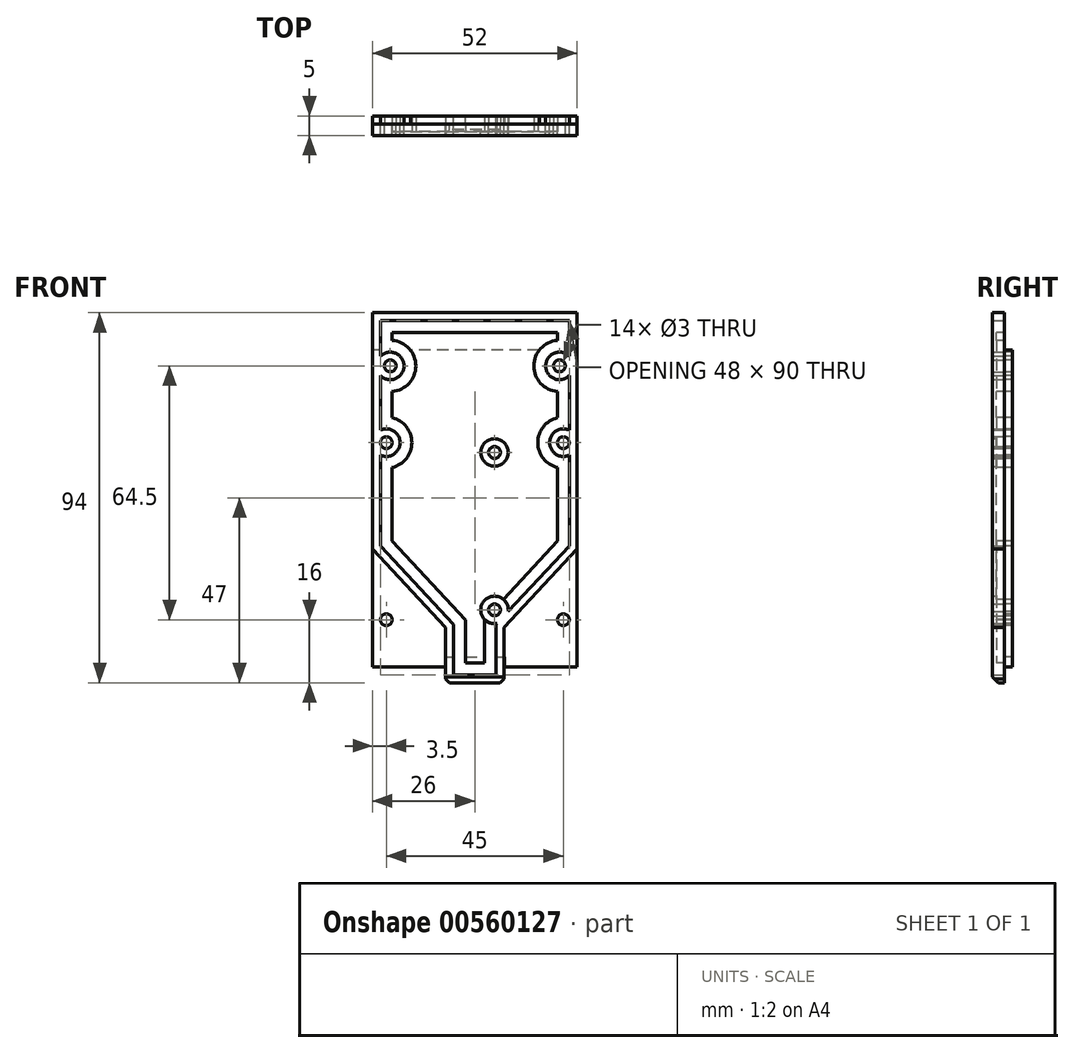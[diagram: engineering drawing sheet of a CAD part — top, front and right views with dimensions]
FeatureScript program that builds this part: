
annotation { "Feature Type Name" : "Feature", "Feature Type Description" : "" }
export const myFeature = defineFeature(function(context is Context, id is Id, definition is map)
    precondition{}
    {
        {
            var Q0;
            Q0=qCreatedBy(makeId("Front.planeOp"),FACE);
            var sketch = newSketch(context, id + "F0", { "sketchPlane" : qUnion([Q0])});
            skLineSegment(sketch, "E0.bottom", {"start": v(26, 40.25) * mm, "end": v(-26, 40.25) * mm});
            skLineSegment(sketch, "E0.top", {"start": v(26, -40.25) * mm, "end": v(-26, -40.25) * mm});
            skLineSegment(sketch, "E0.left", {"start": v(26, 40.25) * mm, "end": v(26, -40.25) * mm});
            skLineSegment(sketch, "E0.right", {"start": v(-26, 40.25) * mm, "end": v(-26, -40.25) * mm});
            skPoint(sketch, "E0.middle", {"position": v(0, 0) * mm});
            skCircle(sketch, "E1", {"center": v(-21.5, 36.25) * mm, "radius": 1.5 * mm});
            skCircle(sketch, "E2", {"center": v(-22.5, 16.75) * mm, "radius": 1.5 * mm});
            skCircle(sketch, "E3", {"center": v(-22.5, -28.25) * mm, "radius": 1.5 * mm});
            skCircle(sketch, "E4.MirrorC", {"center": v(22.5, -28.25) * mm, "radius": 1.5 * mm});
            skCircle(sketch, "E5.MirrorC", {"center": v(22.5, 16.75) * mm, "radius": 1.5 * mm});
            skCircle(sketch, "E6.MirrorC", {"center": v(21.5, 36.25) * mm, "radius": 1.5 * mm});
            skLineSegment(sketch, "E7.bottom", {"start": v(-7.5, -37.75) * mm, "end": v(7.5, -37.75) * mm});
            skLineSegment(sketch, "E7.top", {"start": v(-7.5, -40.25) * mm, "end": v(7.5, -40.25) * mm});
            skLineSegment(sketch, "E7.left", {"start": v(-7.5, -37.75) * mm, "end": v(-7.5, -40.25) * mm});
            skLineSegment(sketch, "E7.right", {"start": v(7.5, -37.75) * mm, "end": v(7.5, -40.25) * mm});
            skCircle(sketch, "E8", {"center": v(5, 14.25) * mm, "radius": 1.5 * mm});
            skCircle(sketch, "E9", {"center": v(5, -25.75) * mm, "radius": 1.5 * mm});
            skSolve(sketch);
        }
        {
            var Q0;
            Q0=makeQuery(id+"F0.imprint","IMPRINT",FACE,{"disambiguationData":[TD([[makeQuery(id+"F0.imprint","IMPRINT",EDGE,{"derivedFrom":sQuery(id+"F0.wireOp",EDGE,"E0.bottom")}),1.0]])]});
            extrude(context, id + "F1", {"entities" : qUnion([Q0]), "oppositeDirection" : true, "depth" : 2 * mm, "offsetDistance" : 25 * mm});
        }
        {
            var Q0;
            Q0=makeQuery(id+"F1.opExtrude","CAP_FACE",FACE,{"disambiguationData":[OSD([sQuery(id+"F0.wireOp",EDGE,"E0.bottom"),sQuery(id+"F0.wireOp",EDGE,"E0.top"),sQuery(id+"F0.wireOp",EDGE,"E0.left"),sQuery(id+"F0.wireOp",EDGE,"E0.right"),sQuery(id+"F0.wireOp",EDGE,"E1"),sQuery(id+"F0.wireOp",EDGE,"E2"),sQuery(id+"F0.wireOp",EDGE,"E3"),sQuery(id+"F0.wireOp",EDGE,"E4.MirrorC"),sQuery(id+"F0.wireOp",EDGE,"E5.MirrorC"),sQuery(id+"F0.wireOp",EDGE,"E6.MirrorC"),sQuery(id+"F0.wireOp",EDGE,"E7.bottom"),sQuery(id+"F0.wireOp",EDGE,"E7.left"),sQuery(id+"F0.wireOp",EDGE,"E7.right")])],"isStart":true});
            var sketch = newSketch(context, id + "F2", { "sketchPlane" : qUnion([Q0])});
            skLineSegment(sketch, "E10.bottom", {"start": v(-26, -40.25) * mm, "end": v(26, -40.25) * mm});
            skLineSegment(sketch, "E10.top", {"start": v(-26, 49.75) * mm, "end": v(26, 49.75) * mm});
            skLineSegment(sketch, "E10.left", {"start": v(-26, -40.25) * mm, "end": v(-26, 49.75) * mm});
            skLineSegment(sketch, "E10.right", {"start": v(26, -40.25) * mm, "end": v(26, 49.75) * mm});
            skLineSegment(sketch, "E11", {"start": v(-26, -10.25) * mm, "end": v(-7.4, -30.25) * mm});
            skLineSegment(sketch, "E12", {"start": v(-7.4, -30.25) * mm, "end": v(-7.4, -44.25) * mm});
            skLineSegment(sketch, "E13", {"start": v(-7.4, -44.25) * mm, "end": v(0, -44.25) * mm});
            skLineSegment(sketch, "E14.MirrorCS", {"start": v(26, -10.25) * mm, "end": v(7.4, -30.25) * mm});
            skLineSegment(sketch, "E15.MirrorCS", {"start": v(7.4, -30.25) * mm, "end": v(7.4, -44.25) * mm});
            skLineSegment(sketch, "E16.MirrorCS", {"start": v(7.4, -44.25) * mm, "end": v(0, -44.25) * mm});
            skSolve(sketch);
        }
        {
            var Q0;
            {var subQ0=sQuery(id+"F2.wireOp",EDGE,"E13");Q0=makeQuery(id+"F2.imprint","IMPRINT",FACE,{"disambiguationData":[TD([[makeQuery(id+"F2.imprint","IMPRINT",EDGE,{"derivedFrom":subQ0}),1.0]])]});}
            var Q1;
            {var subQ0=sQuery(id+"F2.wireOp",EDGE,"E10.top");Q1=makeQuery(id+"F2.imprint","IMPRINT",FACE,{"disambiguationData":[TD([[makeQuery(id+"F2.imprint","IMPRINT",EDGE,{"derivedFrom":subQ0}),-1.0]])]});}
            var Q2;
            {var subQ6=sQuery(id+"F2.wireOp",EDGE,"E11");Q2=makeQuery(id+"F2.imprint","IMPRINT",FACE,{"disambiguationData":[TD([[makeQuery(id+"F2.imprint","IMPRINT",EDGE,{"derivedFrom":subQ6}),1.0]])]});}
            var Q3;
            {var subQ0=sQuery(id+"F2.wireOp",EDGE,"E12");var subQ1=sQuery(id+"F2.wireOp",EDGE,"E10.bottom");var subQ2=makeQuery(id+"F2.imprint","INTERSECT",VERTEX,{"derivedFrom":[subQ1,subQ0]});Q3=makeQuery(id+"F2.imprint","IMPRINT",FACE,{"disambiguationData":[TD([[makeQuery(id+"F2.imprint","IMPRINT",EDGE,{"disambiguationData":[TD([[subQ2,-1.0]])],"derivedFrom":subQ1}),1.0]])]});}
            extrude(context, id + "F3", {"entities" : qUnion([Q0, Q1, Q2, Q3]), "depth" : 3 * mm, "offsetDistance" : 25 * mm});
        }
        {
            var Q0;
            Q0=makeQuery(id+"F3.opExtrude","CAP_FACE",FACE,{"disambiguationData":[OSD([sQuery(id+"F0.wireOp",EDGE,"E1"),sQuery(id+"F0.wireOp",EDGE,"E2"),sQuery(id+"F0.wireOp",EDGE,"E5.MirrorC"),sQuery(id+"F0.wireOp",EDGE,"E6.MirrorC"),sQuery(id+"F2.wireOp",EDGE,"E10.top"),sQuery(id+"F2.wireOp",EDGE,"E10.left"),sQuery(id+"F2.wireOp",EDGE,"E10.right"),sQuery(id+"F2.wireOp",EDGE,"E11"),sQuery(id+"F2.wireOp",EDGE,"E12"),sQuery(id+"F2.wireOp",EDGE,"E13"),sQuery(id+"F2.wireOp",EDGE,"E14.MirrorCS"),sQuery(id+"F2.wireOp",EDGE,"E15.MirrorCS"),sQuery(id+"F2.wireOp",EDGE,"E16.MirrorCS")])],"isStart":false});
            shell(context, id + "F4", {"entities" : qUnion([Q0]), "thickness" : 2 * mm});
        }
        {
            var Q0;
            Q0=makeQuery(id+"F3.opExtrude","CAP_EDGE",EDGE,{"disambiguationData":[OSD([sQuery(id+"F2.wireOp",EDGE,"E13"),sQuery(id+"F2.wireOp",EDGE,"E16.MirrorCS")])],"isStart":false});
            chamfer(context, id + "F5", {"entities" : qUnion([Q0]), "width" : 1.5 * mm, "tangentPropagation" : true});
        }
        {
            var Q0;
            Q0=makeQuery(id+"F3.opExtrude","SWEPT_EDGE",EDGE,{"disambiguationData":[OSD([sQuery(id+"F2.wireOp",EDGE,"E12"),sQuery(id+"F2.wireOp",EDGE,"E13")])]});
            var Q1;
            Q1=makeQuery(id+"F3.opExtrude","SWEPT_EDGE",EDGE,{"disambiguationData":[OSD([sQuery(id+"F2.wireOp",EDGE,"E15.MirrorCS"),sQuery(id+"F2.wireOp",EDGE,"E16.MirrorCS")])]});
            chamfer(context, id + "F6", {"entities" : qUnion([Q0, Q1]), "width" : 1 * mm, "tangentPropagation" : true});
        }
        {
            var Q0;
            Q0=makeQuery(id+"F4.opShell","OFFSET_FACE",FACE,{"disambiguationData":[OSD([sQuery(id+"F0.wireOp",EDGE,"E1"),sQuery(id+"F0.wireOp",EDGE,"E2"),sQuery(id+"F0.wireOp",EDGE,"E5.MirrorC"),sQuery(id+"F0.wireOp",EDGE,"E6.MirrorC"),sQuery(id+"F2.wireOp",EDGE,"E10.top"),sQuery(id+"F2.wireOp",EDGE,"E10.left"),sQuery(id+"F2.wireOp",EDGE,"E10.right"),sQuery(id+"F2.wireOp",EDGE,"E11"),sQuery(id+"F2.wireOp",EDGE,"E12"),sQuery(id+"F2.wireOp",EDGE,"E13"),sQuery(id+"F2.wireOp",EDGE,"E14.MirrorCS"),sQuery(id+"F2.wireOp",EDGE,"E15.MirrorCS"),sQuery(id+"F2.wireOp",EDGE,"E16.MirrorCS")])]});
            var sketch = newSketch(context, id + "F7", { "sketchPlane" : qUnion([Q0])});
            skArc(sketch, "E17.0", {"start": v(21, 10.43) * mm, "mid": v(16, 16.75) * mm, "end": v(21, 23.07) * mm});
            skLineSegment(sketch, "E17.1", {"start": v(21, -8.28) * mm, "end": v(21, 10.43) * mm});
            skLineSegment(sketch, "E17.2", {"start": v(2.4, -28.28) * mm, "end": v(21, -8.28) * mm});
            skLineSegment(sketch, "E17.3", {"start": v(2.4, -39.25) * mm, "end": v(2.4, -28.28) * mm});
            skLineSegment(sketch, "E17.4", {"start": v(-2.4, -39.25) * mm, "end": v(2.4, -39.25) * mm});
            skLineSegment(sketch, "E17.5", {"start": v(-21, 44.75) * mm, "end": v(-21, 42.73) * mm});
            skLineSegment(sketch, "E17.6", {"start": v(21, 44.75) * mm, "end": v(-21, 44.75) * mm});
            skLineSegment(sketch, "E17.7", {"start": v(21, 42.73) * mm, "end": v(21, 44.75) * mm});
            skArc(sketch, "E17.8", {"start": v(21, 29.77) * mm, "mid": v(15, 36.25) * mm, "end": v(21, 42.73) * mm});
            skArc(sketch, "E17.9", {"start": v(-21, 42.73) * mm, "mid": v(-15, 36.25) * mm, "end": v(-21, 29.77) * mm});
            skLineSegment(sketch, "E17.10", {"start": v(-21, 29.77) * mm, "end": v(-21, 23.07) * mm});
            skArc(sketch, "E17.11", {"start": v(-21, 23.07) * mm, "mid": v(-16, 16.75) * mm, "end": v(-21, 10.43) * mm});
            skLineSegment(sketch, "E17.12", {"start": v(-21, 10.43) * mm, "end": v(-21, -8.28) * mm});
            skLineSegment(sketch, "E17.13", {"start": v(-21, -8.28) * mm, "end": v(-2.4, -28.28) * mm});
            skLineSegment(sketch, "E17.14", {"start": v(21, 23.07) * mm, "end": v(21, 29.77) * mm});
            skLineSegment(sketch, "E17.15", {"start": v(-2.4, -28.28) * mm, "end": v(-2.4, -39.25) * mm});
            skSolve(sketch);
        }
        {
            var Q0;
            Q0=makeQuery(id+"F7.imprint","IMPRINT",FACE,{"disambiguationData":[TD([[makeQuery(id+"F7.imprint","IMPRINT",EDGE,{"derivedFrom":sQuery(id+"F7.wireOp",EDGE,"E17.0")}),1.0]])]});
            extrude(context, id + "F8", {"entities" : qUnion([Q0]), "operationType" : NewBodyOperationType.REMOVE, "oppositeDirection" : true, "depth" : 25 * mm, "offsetDistance" : 25 * mm});
        }
    });
